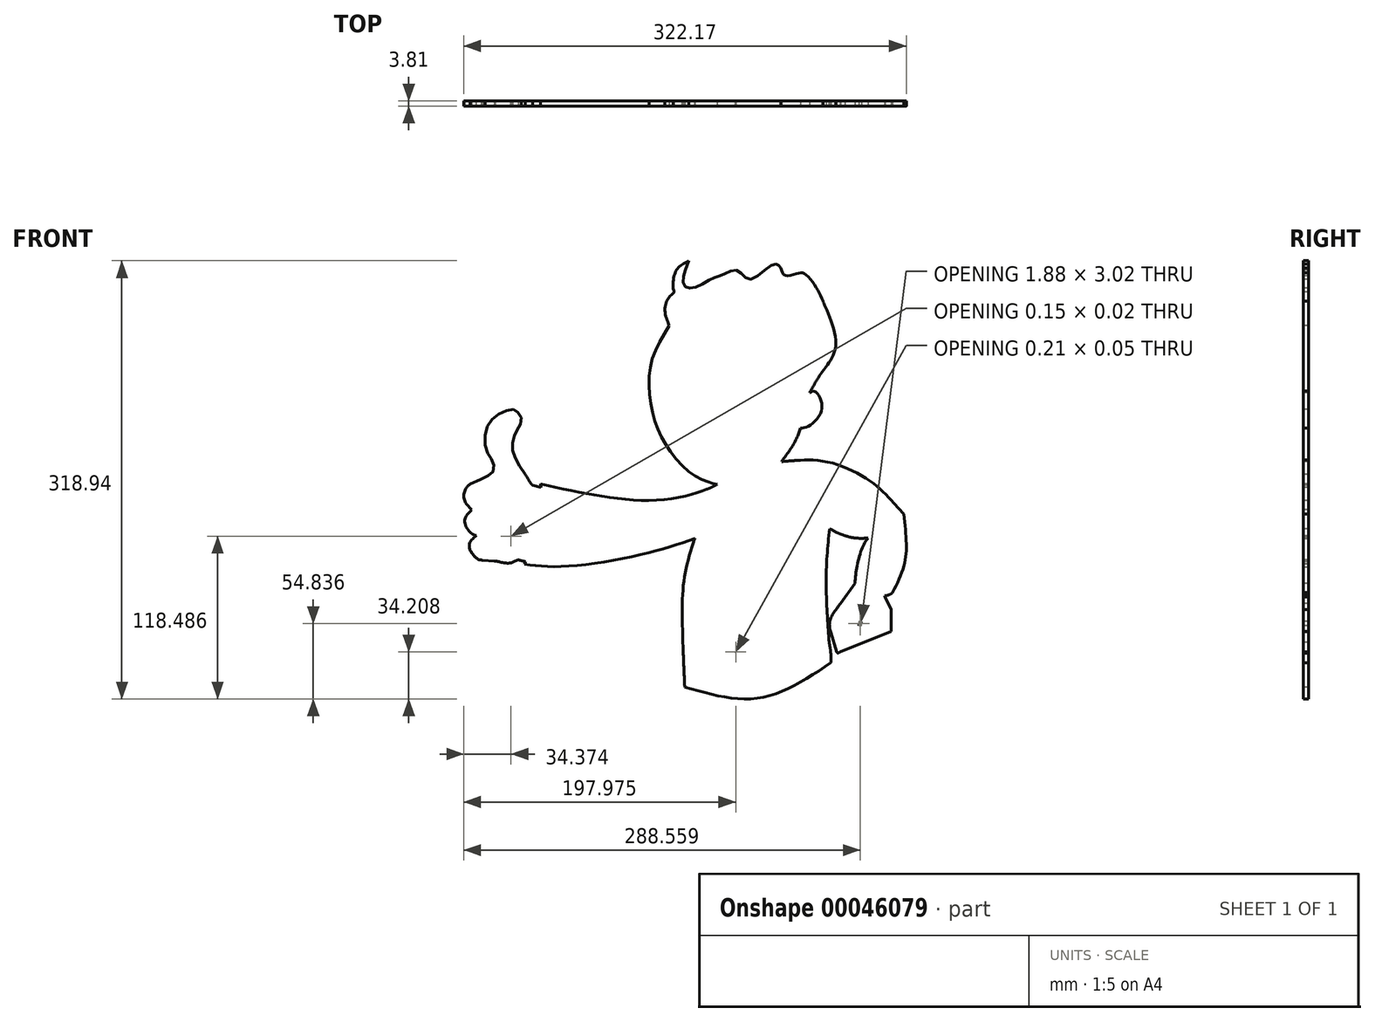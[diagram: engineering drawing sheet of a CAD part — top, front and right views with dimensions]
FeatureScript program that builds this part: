
annotation { "Feature Type Name" : "Feature", "Feature Type Description" : "" }
export const myFeature = defineFeature(function(context is Context, id is Id, definition is map)
    precondition{}
    {
        {
            var Q0;
            Q0=qCreatedBy(makeId("Front.planeOp"),FACE);
            var sketch = newSketch(context, id + "F0", { "sketchPlane" : qUnion([Q0])});
            skFitSpline(sketch, "E0", {"points": [v(50.13, 110.54) * mm, v(59.42, 125.93) * mm, v(69.05, 147.45) * mm, v(59.82, 176.78) * mm, v(59.82, 177.15) * mm], "startDerivative": vector(29.75, 55.27) * mm, "endDerivative": vector(2.31, 5.04) * mm});
            skFitSpline(sketch, "E1", {"points": [v(-32.08, 166.14) * mm, v(-26.7, 166.14) * mm, v(-15.06, 171.52) * mm, v(-4.76, 175.55) * mm, v(2.41, 166.14) * mm, v(16.75, 170.18) * mm, v(24.81, 173.31) * mm, v(31.08, 166.14) * mm, v(33.77, 158.53) * mm, v(35.56, 153.6) * mm, v(48.1, 156.29) * mm, v(57.52, 154.05) * mm, v(51.25, 141.5) * mm, v(44.08, 133.89) * mm], "startDerivative": vector(88.2, -10.9) * mm, "endDerivative": vector(-84.16, -80.95) * mm});
            skFitSpline(sketch, "E2", {"points": [v(44.08, 133.89) * mm, v(54.38, 133.89) * mm, v(62.92, 130.58) * mm], "startDerivative": vector(20.66, 1.85) * mm, "endDerivative": vector(16.64, -8.92) * mm});
            skFitSpline(sketch, "E3", {"points": [v(-47.44, 143.12) * mm, v(-53.66, 138) * mm, v(-54.76, 129.95) * mm, v(-52.93, 123) * mm, v(-47.22, 118.56) * mm, v(-41.77, 124.33) * mm, v(-40.65, 130.58) * mm, v(-42.1, 138.75) * mm, v(-47.44, 143.12) * mm]});
            skFitSpline(sketch, "E4", {"points": [v(-0.6, 133.82) * mm, v(6.36, 138.75) * mm, v(18.44, 133.82) * mm, v(22.47, 129.22) * mm], "startDerivative": vector(18.6, 18.3) * mm, "endDerivative": vector(10.5, -16.47) * mm});
            skFitSpline(sketch, "E5", {"points": [v(-0.6, 133.82) * mm, v(-1.4, 132.75) * mm, v(-0.6, 131.78) * mm, v(1.27, 132.99) * mm, v(2.15, 133.82) * mm, v(3.6, 135.16) * mm, v(6.5, 136.21) * mm, v(11.42, 135.4) * mm, v(15.2, 133.82) * mm], "startDerivative": vector(-12.6, -10.27) * mm, "endDerivative": vector(21.53, -10.19) * mm});
            skFitSpline(sketch, "E6", {"points": [v(15.2, 133.82) * mm, v(16.01, 133.23) * mm, v(19.24, 130.4) * mm, v(20.69, 128.88) * mm, v(21.74, 128.4) * mm, v(22.47, 129.22) * mm], "startDerivative": vector(4.24, -2.9) * mm, "endDerivative": vector(4.07, 7.17) * mm});
            skFitSpline(sketch, "E7", {"points": [v(-21.75, 134.43) * mm, v(-25.48, 123.23) * mm, v(-35.27, 105.04) * mm, v(-35.97, 103.17) * mm, v(-35.27, 100.37) * mm, v(-32.24, 96.64) * mm, v(-31.3, 94.77) * mm], "startDerivative": vector(-10.07, -41.5) * mm, "endDerivative": vector(6.38, -17.85) * mm});
            skFitSpline(sketch, "E8", {"points": [v(-21.75, 134.43) * mm, v(-24.78, 119.73) * mm, v(-28.74, 108.77) * mm, v(-29.44, 103.4) * mm], "startDerivative": vector(-5.78, -37.33) * mm, "endDerivative": vector(-0.9, -20.57) * mm});
            skFitSpline(sketch, "E9", {"points": [v(-29.44, 103.4) * mm, v(-24.31, 96.87) * mm], "startDerivative": vector(5.13, -6.53) * mm, "endDerivative": vector(5.13, -6.53) * mm});
            skFitSpline(sketch, "E10", {"points": [v(-35.27, 82.18) * mm, v(-36.67, 76.11) * mm, v(-33.18, 65.15) * mm, v(-42.04, 73.55) * mm, v(-35.27, 82.18) * mm]});
            skLineSegment(sketch, "E11", {"start": v(-24.31, 96.87) * mm, "end": v(-31.3, 94.77) * mm});
            skFitSpline(sketch, "E12", {"points": [v(-36.33, 78.76) * mm, v(-18.4, 77.61) * mm, v(-2.48, 81.02) * mm, v(-2.48, 81.11) * mm], "startDerivative": vector(32.43, -5.7) * mm, "endDerivative": vector(-1.31, 2.33) * mm});
            skFitSpline(sketch, "E13", {"points": [v(-33.18, 66.5) * mm, v(-27.23, 65.15) * mm, v(-7.82, 65.15) * mm, v(7.83, 73.93) * mm], "startDerivative": vector(22, -6.15) * mm, "endDerivative": vector(37.03, 28.65) * mm});
            skFitSpline(sketch, "E14", {"points": [v(-2.46, 81.08) * mm, v(1.2, 82.95) * mm], "startDerivative": vector(3.67, 1.87) * mm, "endDerivative": vector(3.67, 1.87) * mm});
            skFitSpline(sketch, "E15", {"points": [v(1.2, 82.95) * mm, v(1.2, 84.33) * mm, v(2.12, 86.63) * mm, v(4.42, 86.82) * mm, v(8.56, 85.07) * mm, v(11.42, 83.87) * mm, v(13.53, 79.91) * mm, v(13.35, 75.77) * mm, v(12.52, 73.38) * mm, v(11.42, 74.67) * mm, v(11.42, 76.88) * mm, v(10.87, 79.73) * mm, v(10.04, 81.02) * mm, v(5.34, 82.3) * mm, v(1.2, 82.95) * mm]});
            skFitSpline(sketch, "E16", {"points": [v(7.83, 73.93) * mm, v(10.59, 76.88) * mm], "startDerivative": vector(2.76, 2.94) * mm, "endDerivative": vector(2.76, 2.94) * mm});
            skFitSpline(sketch, "E17", {"points": [v(60.14, 126.9) * mm, v(56.3, 128.64) * mm, v(46.2, 131) * mm, v(44.44, 130.67) * mm, v(44.1, 129.59) * mm, v(45.05, 129.31) * mm, v(48.5, 128.64) * mm, v(54.26, 127.35) * mm, v(58.83, 125.11) * mm], "startDerivative": vector(-22.37, 12.58) * mm, "endDerivative": vector(29.2, -17) * mm});
            skFitSpline(sketch, "E18", {"points": [v(57.45, 123.12) * mm, v(56.23, 124.5) * mm, v(49.05, 126.6) * mm, v(46.2, 126.94) * mm, v(45.66, 126.2) * mm, v(46.33, 125.25) * mm, v(49.11, 124.77) * mm, v(54.13, 123.62) * mm, v(56.59, 121.8) * mm], "startDerivative": vector(-7.37, 14.27) * mm, "endDerivative": vector(16.28, -15.48) * mm});
            skFitSpline(sketch, "E19", {"points": [v(45.72, 119.76) * mm, v(44.3, 120.03) * mm, v(44.44, 121.18) * mm, v(47.83, 121.18) * mm, v(50.33, 120.44) * mm, v(51.55, 119.49) * mm, v(51.82, 118.4) * mm, v(50.67, 118.13) * mm, v(49.25, 118.95) * mm, v(47.42, 119.42) * mm, v(45.72, 119.76) * mm]});
            skFitSpline(sketch, "E20", {"points": [v(42.81, 115.67) * mm, v(45.72, 115.67) * mm, v(49.45, 114) * mm], "startDerivative": vector(6.25, 0.7) * mm, "endDerivative": vector(7.01, -3.9) * mm});
            skFitSpline(sketch, "E21", {"points": [v(42.81, 115.67) * mm, v(42.2, 115.08) * mm, v(42.81, 114.88) * mm, v(43.76, 114.88) * mm, v(44.84, 114.95) * mm, v(46.06, 114.81) * mm, v(48.18, 114) * mm, v(48.97, 113.67) * mm, v(49.45, 113.74) * mm, v(49.45, 114) * mm], "startDerivative": vector(-8.93, -6.16) * mm, "endDerivative": vector(-1.3, 4.9) * mm});
            skFitSpline(sketch, "E22", {"points": [v(-15.65, 58.15) * mm, v(-11.91, 58.75) * mm, v(-6.83, 60.7) * mm, v(-5.63, 59.5) * mm, v(-5.04, 57.7) * mm, v(-7.28, 57.1) * mm, v(-11.02, 57.1) * mm, v(-15.65, 58.15) * mm]});
            skFitSpline(sketch, "E23", {"points": [v(-53.58, 144.28) * mm, v(-52.5, 144.07) * mm, v(-48.8, 146.02) * mm, v(-42.6, 149.29) * mm, v(-39.22, 150.38) * mm], "startDerivative": vector(7.02, -3.06) * mm, "endDerivative": vector(12.56, 3.33) * mm});
            skFitSpline(sketch, "E24", {"points": [v(-53.58, 144.28) * mm, v(-53.58, 145.26) * mm, v(-44.66, 150.38) * mm], "startDerivative": vector(-1.38, 3.85) * mm, "endDerivative": vector(16.14, 7.66) * mm});
            skFitSpline(sketch, "E25", {"points": [v(-44.66, 150.38) * mm, v(-39.44, 152.34) * mm, v(-37.92, 151.9) * mm, v(-37.59, 151.25) * mm, v(-39.22, 150.38) * mm], "startDerivative": vector(14.6, 6.93) * mm, "endDerivative": vector(-9.7, -3.42) * mm});
            skFitSpline(sketch, "E26", {"points": [v(8.7, 154.3) * mm, v(7.32, 153.67) * mm, v(6.69, 152.22) * mm, v(6.82, 151.03) * mm, v(7, 150.97) * mm], "startDerivative": vector(-5.03, -1.45) * mm, "endDerivative": vector(1.83, 0) * mm});
            skFitSpline(sketch, "E27", {"points": [v(7, 150.97) * mm, v(7.82, 150.46) * mm, v(10.78, 150.09) * mm, v(14.04, 148.96) * mm, v(16.94, 147.07) * mm, v(19.45, 144.74) * mm, v(20.96, 142.86) * mm, v(22.72, 143.68) * mm, v(22.15, 145.62) * mm, v(20.2, 148.64) * mm, v(17.5, 150.97) * mm, v(13.98, 153.48) * mm, v(10.27, 154.61) * mm, v(8.7, 154.3) * mm], "startDerivative": vector(14.48, -12.75) * mm, "endDerivative": vector(-23.85, -8.4) * mm});
            skFitSpline(sketch, "E28", {"points": [v(-17.29, 43.67) * mm, v(-14.75, 40.26) * mm, v(0.53, 36.43) * mm, v(24.24, 42.28) * mm, v(29.61, 55.12) * mm, v(29.61, 60.02) * mm], "startDerivative": vector(13.91, -29.26) * mm, "endDerivative": vector(-2.2, 31.94) * mm});
            skFitSpline(sketch, "E29", {"points": [v(29.61, 60.02) * mm, v(29.61, 60.9) * mm], "startDerivative": vector(0, 0.88) * mm, "endDerivative": vector(0, 0.88) * mm});
            skFitSpline(sketch, "E30", {"points": [v(-33.78, 4) * mm, v(-40.9, -22.22) * mm, v(-42.7, -53.76) * mm, v(-40.9, -103.78) * mm], "startDerivative": vector(-28.62, -88.9) * mm, "endDerivative": vector(6.18, -133.53) * mm});
            skFitSpline(sketch, "E31", {"points": [v(64.54, 11.47) * mm, v(62.05, -23.4) * mm, v(64.23, -71.35) * mm], "startDerivative": vector(-7.58, -72.7) * mm, "endDerivative": vector(6.59, -92.41) * mm});
            skFitSpline(sketch, "E32", {"points": [v(29.61, 60.31) * mm, v(37.36, 60.9) * mm, v(61.6, 60.31) * mm, v(94.7, 45.73) * mm, v(111.2, 30.12) * mm], "startDerivative": vector(44.64, 3.25) * mm, "endDerivative": vector(55.06, -61.44) * mm});
            skFitSpline(sketch, "E33", {"points": [v(75.86, 6.32) * mm, v(82.98, 4.7) * mm, v(92.43, 4.6) * mm], "startDerivative": vector(14.64, -4.26) * mm, "endDerivative": vector(18.43, 0.72) * mm});
            skFitSpline(sketch, "E34", {"points": [v(111.2, 30.12) * mm, v(118.49, 22.03) * mm], "startDerivative": vector(7.3, -8.1) * mm, "endDerivative": vector(7.3, -8.1) * mm});
            skFitSpline(sketch, "E35", {"points": [v(92.43, 4.6) * mm, v(89.16, -0.64) * mm, v(84.7, -14.75) * mm, v(82.98, -28.23) * mm], "startDerivative": vector(-13.12, -17.8) * mm, "endDerivative": vector(-2.92, -35.34) * mm});
            skFitSpline(sketch, "E36", {"points": [v(82.98, -28.23) * mm, v(72.5, -42.99) * mm], "startDerivative": vector(-10.48, -14.76) * mm, "endDerivative": vector(-10.48, -14.76) * mm});
            skFitSpline(sketch, "E37", {"points": [v(65.44, -64.38) * mm, v(69.72, -78.18) * mm], "startDerivative": vector(4.28, -13.8) * mm, "endDerivative": vector(4.28, -13.8) * mm});
            skFitSpline(sketch, "E38", {"points": [v(72.33, -78.18) * mm, v(109.5, -63.22) * mm], "startDerivative": vector(37.16, 14.96) * mm, "endDerivative": vector(37.16, 14.96) * mm});
            skFitSpline(sketch, "E39", {"points": [v(109.5, -63.22) * mm, v(109.5, -47.36) * mm], "startDerivative": vector(0, 15.86) * mm, "endDerivative": vector(0, 15.86) * mm});
            skFitSpline(sketch, "E40", {"points": [v(109.5, -47.36) * mm, v(104.96, -38.07) * mm], "startDerivative": vector(-4.53, 9.3) * mm, "endDerivative": vector(-4.53, 9.3) * mm});
            skFitSpline(sketch, "E41", {"points": [v(104.77, -41.17) * mm, v(91.36, -50.08) * mm, v(91.36, -50.53) * mm], "startDerivative": vector(-22.36, -13.52) * mm, "endDerivative": vector(1.12, -2.63) * mm});
            skFitSpline(sketch, "E42", {"points": [v(91.36, -50.08) * mm, v(85.93, -59.14) * mm], "startDerivative": vector(-5.44, -9.06) * mm, "endDerivative": vector(-5.44, -9.06) * mm});
            skFitSpline(sketch, "E43", {"points": [v(87.74, -56.12) * mm, v(85.93, -59.14) * mm, v(95, -59.14) * mm], "startDerivative": vector(-8.45, -9.38) * mm, "endDerivative": vector(20.7, 2.42) * mm});
            skFitSpline(sketch, "E44", {"points": [v(95, -58.7) * mm, v(98.62, -52.8) * mm], "startDerivative": vector(3.63, 5.9) * mm, "endDerivative": vector(3.63, 5.9) * mm});
            skFitSpline(sketch, "E45", {"points": [v(105.06, -38.26) * mm, v(104.56, -37.13) * mm], "startDerivative": vector(-0.5, 1.13) * mm, "endDerivative": vector(-0.5, 1.13) * mm});
            skFitSpline(sketch, "E46", {"points": [v(69.72, -78.18) * mm, v(70.41, -79) * mm, v(72.33, -78.18) * mm], "startDerivative": vector(1.32, -2.65) * mm, "endDerivative": vector(3.77, 2.37) * mm});
            skFitSpline(sketch, "E47", {"points": [v(110.17, -33.85) * mm, v(110.16, -33.84) * mm], "startDerivative": vector(0, 0) * mm, "endDerivative": vector(0, 0) * mm});
            skFitSpline(sketch, "E48", {"points": [v(-33.78, 4) * mm, v(-33.57, 4.26) * mm], "startDerivative": vector(0.18, 0.3) * mm, "endDerivative": vector(0.18, 0.3) * mm});
            skFitSpline(sketch, "E49", {"points": [v(-40.9, -103.78) * mm, v(13.5, -111.72) * mm, v(65.41, -86.24) * mm], "startDerivative": vector(112.06, -32.49) * mm, "endDerivative": vector(100.6, 67.15) * mm});
            skFitSpline(sketch, "E50", {"points": [v(64.23, -71.35) * mm, v(65.41, -79) * mm, v(65.41, -86.24) * mm], "startDerivative": vector(2.92, -15.13) * mm, "endDerivative": vector(-0.57, -14.64) * mm});
            skFitSpline(sketch, "E51", {"points": [v(-42.13, -75) * mm, v(-16.18, -79.13) * mm, v(27.63, -70.95) * mm, v(52.32, -59.13) * mm, v(62.83, -50.46) * mm], "startDerivative": vector(94.94, -25.3) * mm, "endDerivative": vector(54.09, 48.22) * mm});
            skFitSpline(sketch, "E52", {"points": [v(-41.47, -91.12) * mm, v(-18.12, -96.3) * mm, v(18.32, -93.46) * mm, v(50.3, -79.94) * mm, v(64.52, -72.9) * mm], "startDerivative": vector(92.5, -27.07) * mm, "endDerivative": vector(66.9, 32.65) * mm});
            skFitSpline(sketch, "E53", {"points": [v(0.53, 26.25) * mm, v(-4.3, 0.08) * mm, v(-8.09, -30.58) * mm, v(-5.36, -64.6) * mm, v(-3.68, -78.24) * mm, v(-3.89, -78.27) * mm], "startDerivative": vector(-19.33, -103.38) * mm, "endDerivative": vector(-10.4, 2.62) * mm});
            skFitSpline(sketch, "E54", {"points": [v(21.54, 27.5) * mm, v(16.27, 5.96) * mm, v(13.12, -17.56) * mm, v(11.44, -35) * mm, v(12.91, -52.84) * mm, v(16.48, -74.27) * mm], "startDerivative": vector(-28.05, -100.99) * mm, "endDerivative": vector(18.76, -106.08) * mm});
            skFitSpline(sketch, "E55", {"points": [v(43.22, 61.3) * mm, v(42.44, 49.4) * mm, v(33.94, 36.02) * mm, v(21.54, 27.5) * mm], "startDerivative": vector(2.05, -38.27) * mm, "endDerivative": vector(-37.8, -21.41) * mm});
            skFitSpline(sketch, "E56", {"points": [v(-145.77, 44.08) * mm, v(-99.83, 34.78) * mm, v(-53.62, 32.83) * mm, v(-24.87, 40.17) * mm, v(-17.29, 43.67) * mm], "startDerivative": vector(145.84, -33.23) * mm, "endDerivative": vector(48.2, 24.73) * mm});
            skFitSpline(sketch, "E57", {"points": [v(-156.74, -12.52) * mm, v(-161.16, -11.46) * mm, v(-162.17, -11.16) * mm], "startDerivative": vector(-7.13, 1.61) * mm, "endDerivative": vector(-2.2, -0.18) * mm});
            skFitSpline(sketch, "E58", {"points": [v(-145.53, 41.63) * mm, v(-151.61, 42.93) * mm], "startDerivative": vector(-5.81, 1.25) * mm, "endDerivative": vector(-5.81, 1.25) * mm});
            skFitSpline(sketch, "E59", {"points": [v(-152.1, 13.65) * mm, v(-152.56, 13.96) * mm, v(-153.22, 14.24) * mm], "startDerivative": vector(-0.82, 0.82) * mm, "endDerivative": vector(-1.34, 0.38) * mm});
            skFitSpline(sketch, "E60", {"points": [v(-153.22, 14.24) * mm, v(-152.6, 14.2) * mm, v(-151.54, 14.49) * mm], "startDerivative": vector(1.37, -0.2) * mm, "endDerivative": vector(1.96, 0.66) * mm});
            skFitSpline(sketch, "E61", {"points": [v(-189, -11.33) * mm, v(-192.36, -10.14) * mm, v(-197.81, -1.13) * mm, v(-192.6, 6.51) * mm], "startDerivative": vector(-13.42, -0.8) * mm, "endDerivative": vector(21.15, 18.09) * mm});
            skFitSpline(sketch, "E62", {"points": [v(-192.6, 6.51) * mm, v(-195.44, 7.4) * mm, v(-201.13, 16.66) * mm, v(-195.91, 25.24) * mm], "startDerivative": vector(-11.37, -0.03) * mm, "endDerivative": vector(20.78, 19.91) * mm});
            skFitSpline(sketch, "E63", {"points": [v(-151.54, 14.49) * mm, v(-150.68, 14.7) * mm, v(-148.1, 19.04) * mm, v(-147.1, 25.9) * mm, v(-147.4, 37.26) * mm, v(-147.4, 37.4) * mm], "startDerivative": vector(8.17, -0.43) * mm, "endDerivative": vector(0.09, 1.86) * mm});
            skFitSpline(sketch, "E64", {"points": [v(-147.4, 37.4) * mm, v(-147.8, 39.01) * mm, v(-149.54, 41.18) * mm, v(-151.61, 42.93) * mm], "startDerivative": vector(-0.72, 5.61) * mm, "endDerivative": vector(-5.82, 4.56) * mm});
            skFitSpline(sketch, "E65", {"points": [v(-151.61, 42.93) * mm, v(-152.66, 44.09) * mm, v(-157.02, 51) * mm], "startDerivative": vector(-2.81, 2.98) * mm, "endDerivative": vector(-7.66, 11.82) * mm});
            skFitSpline(sketch, "E66", {"points": [v(-197.17, 43.98) * mm, v(-183.66, 50.12) * mm, v(-179.9, 54.02) * mm, v(-180.97, 61.15) * mm, v(-184.47, 66.4) * mm, v(-186.22, 78.5) * mm, v(-182.45, 89.53) * mm, v(-174.51, 95.85) * mm, v(-165.9, 98.23) * mm, v(-162.03, 95.69) * mm, v(-159.84, 90.86) * mm, v(-162.3, 84.42) * mm, v(-165.04, 78.84) * mm, v(-166.36, 71.37) * mm, v(-164.2, 62.86) * mm, v(-157.02, 51) * mm], "startDerivative": vector(180.37, 86.36) * mm, "endDerivative": vector(95.72, -136.07) * mm});
            skFitSpline(sketch, "E67", {"points": [v(-195.91, 25.24) * mm, v(-170.12, 24.3) * mm], "startDerivative": vector(25.8, -0.95) * mm, "endDerivative": vector(25.8, -0.95) * mm});
            skFitSpline(sketch, "E68", {"points": [v(-166.9, 24.18) * mm, v(-161.58, 21.84) * mm, v(-160.2, 11.2) * mm, v(-164.29, 6.67) * mm, v(-192.6, 6.51) * mm], "startDerivative": vector(33.91, -4.89) * mm, "endDerivative": vector(-87.46, 5.9) * mm});
            skFitSpline(sketch, "E69", {"points": [v(-192.6, 6.51) * mm, v(-167.46, 6) * mm, v(-167.31, 6.03) * mm], "startDerivative": vector(38.67, -0.96) * mm, "endDerivative": vector(1.14, 0.36) * mm});
            skFitSpline(sketch, "E70", {"points": [v(-197.17, 43.98) * mm, v(-197.16, 43.92) * mm, v(-197.21, 43.96) * mm], "startDerivative": vector(-0.03, -0.02) * mm, "endDerivative": vector(-0.05, -0.03) * mm});
            skFitSpline(sketch, "E71", {"points": [v(-166.9, 24.18) * mm, v(-167.19, 24.16) * mm, v(-167.4, 24.24) * mm], "startDerivative": vector(-0.57, 0.07) * mm, "endDerivative": vector(-0.4, 0.06) * mm});
            skFitSpline(sketch, "E72", {"points": [v(-37.9, 206.47) * mm, v(-40.58, 199.07) * mm, v(-41.45, 188.92) * mm, v(-35.07, 186.6) * mm, v(-21.44, 193.27) * mm, v(-12.45, 196.75) * mm, v(-2.59, 199.36) * mm, v(5.83, 192.98) * mm, v(21.78, 202.84) * mm, v(27, 203.42) * mm, v(29.03, 201.1) * mm], "startDerivative": vector(-28.8, -72.3) * mm, "endDerivative": vector(29.74, -46.45) * mm});
            skFitSpline(sketch, "E73", {"points": [v(29.03, 201.1) * mm, v(32.22, 195.88) * mm, v(41.8, 197.33) * mm, v(46.14, 197.04) * mm, v(54.26, 188.05) * mm, v(59.82, 177.15) * mm], "startDerivative": vector(11.35, -40.23) * mm, "endDerivative": vector(19.55, -44.97) * mm});
            skFitSpline(sketch, "E74", {"points": [v(-189, -11.33) * mm, v(-188.14, -11.56) * mm], "startDerivative": vector(0.85, -0.29) * mm, "endDerivative": vector(0.85, -0.29) * mm});
            skFitSpline(sketch, "E75", {"points": [v(-179.52, -12.07) * mm, v(-178.5, -12.07) * mm, v(-169.81, -13.61) * mm, v(-161.93, -11.14) * mm], "startDerivative": vector(6.5, 0.95) * mm, "endDerivative": vector(24.22, 10.12) * mm});
            skFitSpline(sketch, "E76", {"points": [v(-161.93, -11.14) * mm, v(-155.9, -6.95) * mm, v(-153.19, -2.2) * mm, v(-151.97, 5.81) * mm, v(-152.1, 13.65) * mm], "startDerivative": vector(21.28, 21.91) * mm, "endDerivative": vector(-1.06, 28.7) * mm});
            skFitSpline(sketch, "E77", {"points": [v(-24.87, 40.17) * mm, v(-22.24, 35.54) * mm, v(-8.09, 27.34) * mm, v(0.53, 26.25) * mm], "startDerivative": vector(5.88, -17.7) * mm, "endDerivative": vector(24.32, 0.18) * mm});
            skFitSpline(sketch, "E78", {"points": [v(-32.08, 166.14) * mm, v(-36.7, 167.93) * mm, v(-41.64, 170.56) * mm], "startDerivative": vector(-9.85, 2.76) * mm, "endDerivative": vector(-7.14, 8.19) * mm});
            skFitSpline(sketch, "E79", {"points": [v(-48.62, 183.8) * mm, v(-52, 180.15) * mm, v(-55.34, 169.96) * mm, v(-52.23, 159.14) * mm], "startDerivative": vector(-7.04, -13.73) * mm, "endDerivative": vector(5.31, -16.1) * mm});
            skFitSpline(sketch, "E80", {"points": [v(-197.16, 43.92) * mm, v(-200.07, 40.94) * mm, v(-201.59, 33.35) * mm, v(-195.91, 25.24) * mm], "startDerivative": vector(-11.93, -9.3) * mm, "endDerivative": vector(19.13, -19.37) * mm});
            skFitSpline(sketch, "E81", {"points": [v(-197.16, 43.92) * mm, v(-175, 43.92) * mm, v(-164.96, 40.84) * mm, v(-160.78, 30.34) * mm, v(-164.73, 25.15) * mm, v(-166.9, 24.18) * mm, v(-170.12, 24.3) * mm], "startDerivative": vector(88.21, 1.7) * mm, "endDerivative": vector(-33.47, 3.56) * mm});
            skFitSpline(sketch, "E82", {"points": [v(-145.77, 44.08) * mm, v(-145.53, 41.63) * mm], "startDerivative": vector(0.23, -2.45) * mm, "endDerivative": vector(0.23, -2.45) * mm});
            skFitSpline(sketch, "E83", {"points": [v(-157.65, -14.45) * mm, v(-156.74, -12.52) * mm], "startDerivative": vector(0.92, 1.93) * mm, "endDerivative": vector(0.92, 1.93) * mm});
            skFitSpline(sketch, "E84", {"points": [v(-156.74, -12.52) * mm, v(-149.44, 0) * mm, v(-144.45, 13.1) * mm, v(-145.53, 41.63) * mm], "startDerivative": vector(25.63, 42.98) * mm, "endDerivative": vector(-8.16, 75.99) * mm});
            skFitSpline(sketch, "E85", {"points": [v(75.86, 6.32) * mm, v(71.26, 8.02) * mm, v(64.54, 11.47) * mm], "startDerivative": vector(-9.9, 3.26) * mm, "endDerivative": vector(-12.64, 6.9) * mm});
            skFitSpline(sketch, "E86", {"points": [v(64.54, 11.47) * mm, v(63.72, 12.05) * mm, v(61.99, 13.69) * mm], "startDerivative": vector(-1.93, 1.25) * mm, "endDerivative": vector(-3.09, 3.06) * mm});
            skFitSpline(sketch, "E87", {"points": [v(72.5, -42.99) * mm, v(68.2, -48.82) * mm, v(64.59, -56.32) * mm, v(65.44, -64.38) * mm], "startDerivative": vector(-13.37, -17.43) * mm, "endDerivative": vector(5.8, -24.1) * mm});
            skFitSpline(sketch, "E88", {"points": [v(104.77, -41.17) * mm, v(105.75, -40.64) * mm, v(106.47, -41.17) * mm], "startDerivative": vector(1.95, 1.54) * mm, "endDerivative": vector(1.44, -1.6) * mm});
            skFitSpline(sketch, "E89", {"points": [v(-157.65, -14.45) * mm, v(-128.26, -15.97) * mm, v(-68.84, -6.4) * mm, v(-33.57, 4.26) * mm], "startDerivative": vector(92.4, -11.33) * mm, "endDerivative": vector(100.31, 34.14) * mm});
            skFitSpline(sketch, "E90", {"points": [v(82.98, -28.23) * mm, v(85.19, -30.53) * mm, v(95.75, -34.92) * mm, v(104.56, -37.13) * mm], "startDerivative": vector(7.12, -10.3) * mm, "endDerivative": vector(22.19, -4.83) * mm});
            skFitSpline(sketch, "E91", {"points": [v(104.56, -37.13) * mm, v(106.4, -37.13) * mm, v(109.68, -35.69) * mm, v(110.45, -35.04) * mm], "startDerivative": vector(5.08, -0.79) * mm, "endDerivative": vector(2.4, 2.48) * mm});
            skFitSpline(sketch, "E92", {"points": [v(118.49, 22.03) * mm, v(120.4, 0) * mm, v(118.49, -16.17) * mm, v(110.45, -35.04) * mm], "startDerivative": vector(7.53, -64.86) * mm, "endDerivative": vector(-27.6, -56.45) * mm});
            skFitSpline(sketch, "E93", {"points": [v(43.38, 84.78) * mm, v(39.44, 74.98) * mm, v(29.61, 60.31) * mm], "startDerivative": vector(-7.22, -21.7) * mm, "endDerivative": vector(-19.79, -27.01) * mm});
            skFitSpline(sketch, "E94", {"points": [v(29.61, 60.31) * mm, v(28.9, 59.33) * mm, v(27.2, 58.02) * mm, v(27.18, 58) * mm], "startDerivative": vector(-1.06, -2.15) * mm, "endDerivative": vector(-0.08, -0.13) * mm});
            skFitSpline(sketch, "E95", {"points": [v(-17.29, 43.67) * mm, v(-23.81, 45.38) * mm, v(-37.25, 52.37) * mm, v(-53.03, 70.12) * mm, v(-62.52, 89.43) * mm, v(-66.83, 113.26) * mm, v(-64, 136.56) * mm, v(-52.23, 159.14) * mm], "startDerivative": vector(-71.14, 15.45) * mm, "endDerivative": vector(78.93, 135.15) * mm});
            skFitSpline(sketch, "E96", {"points": [v(-52.23, 159.14) * mm, v(-46.86, 166.35) * mm, v(-41.64, 170.56) * mm], "startDerivative": vector(9.66, 14.61) * mm, "endDerivative": vector(11.57, 8.08) * mm});
            skFitSpline(sketch, "E97", {"points": [v(-17.29, 43.67) * mm, v(-12.79, 43.12) * mm, v(-10.72, 43.08) * mm], "startDerivative": vector(4.13, -1.26) * mm, "endDerivative": vector(3.89, -0.12) * mm});
            skFitSpline(sketch, "E98", {"points": [v(50.13, 110.54) * mm, v(53.61, 111.45) * mm, v(58.27, 105.04) * mm, v(57.6, 94.74) * mm, v(48.8, 85.84) * mm, v(43.38, 84.78) * mm], "startDerivative": vector(24.96, 14.11) * mm, "endDerivative": vector(-29.77, -0.66) * mm});
            skFitSpline(sketch, "E99", {"points": [v(50.13, 110.54) * mm, v(48.62, 109.78) * mm, v(47.13, 108.54) * mm, v(46.8, 107.95) * mm], "startDerivative": vector(-3.96, -1.72) * mm, "endDerivative": vector(-0.97, -2.31) * mm});
            skLineSegment(sketch, "E100", {"start": v(-188.14, -11.56) * mm, "end": v(-179.52, -12.07) * mm});
            skLineSegment(sketch, "E101", {"start": v(-179.2, -12.03) * mm, "end": v(-166.1, -12.07) * mm});
            skFitSpline(sketch, "E102", {"points": [v(-167.3, 6.03) * mm, v(-162.34, 4.76) * mm, v(-160.76, -2.98) * mm, v(-162.1, -8.55) * mm, v(-166.1, -12.07) * mm], "startDerivative": vector(24.78, -0.12) * mm, "endDerivative": vector(-19.59, -13.52) * mm});
            skFitSpline(sketch, "E103", {"points": [v(-37.9, 206.47) * mm, v(-45.23, 201.8) * mm, v(-48.22, 196.8) * mm, v(-49.5, 187.52) * mm, v(-48.62, 183.8) * mm], "startDerivative": vector(-29.17, -15.9) * mm, "endDerivative": vector(6.26, -16.7) * mm});
            skFitSpline(sketch, "E104", {"points": [v(-48.62, 183.8) * mm, v(-47.15, 179.74) * mm, v(-43.2, 172.92) * mm, v(-41.64, 170.56) * mm], "startDerivative": vector(3.33, -11.6) * mm, "endDerivative": vector(5.22, -7.62) * mm});
            skSolve(sketch);
        }
        {
            var Q0;
            Q0 = qSketchRegion(id + "F0", true);
            extrude(context, id + "F1", {"entities" : qUnion([Q0]), "oppositeDirection" : true, "depth" : 3.8 * mm});
        }
        {
            var Q0;
            {var subQ0=sQuery(id+"F0.wireOp",EDGE,"E10");var subQ1=makeQuery(id+"F0.imprint","IMPRINT",VERTEX,{"disambiguationData":[OD(0.0)],"derivedFrom":subQ0});Q0=makeQuery(id+"F0.imprint","IMPRINT",FACE,{"disambiguationData":[TD([[makeQuery(id+"F0.imprint","IMPRINT",EDGE,{"disambiguationData":[TD([[subQ1,-1.0]])],"derivedFrom":subQ0}),-1.0]])]});}
            var Q1;
            Q1=makeQuery(id+"F0.imprint","IMPRINT",FACE,{"disambiguationData":[TD([[makeQuery(id+"F0.imprint","IMPRINT",EDGE,{"derivedFrom":sQuery(id+"F0.wireOp",EDGE,"E22")}),-1.0]])]});
            var Q2;
            Q2=makeQuery(id+"F0.imprint","IMPRINT",FACE,{"disambiguationData":[TD([[makeQuery(id+"F0.imprint","IMPRINT",EDGE,{"derivedFrom":sQuery(id+"F0.wireOp",EDGE,"E15")}),-1.0]])]});
            var Q3;
            Q3=makeQuery(id+"F0.imprint","IMPRINT",FACE,{"disambiguationData":[TD([[makeQuery(id+"F0.imprint","IMPRINT",EDGE,{"derivedFrom":sQuery(id+"F0.wireOp",EDGE,"E7")}),1.0]])]});
            var Q4;
            Q4=makeQuery(id+"F0.imprint","IMPRINT",FACE,{"disambiguationData":[TD([[makeQuery(id+"F0.imprint","IMPRINT",EDGE,{"derivedFrom":sQuery(id+"F0.wireOp",EDGE,"E20")}),-1.0]])]});
            var Q5;
            Q5=makeQuery(id+"F0.imprint","IMPRINT",FACE,{"disambiguationData":[TD([[makeQuery(id+"F0.imprint","IMPRINT",EDGE,{"derivedFrom":sQuery(id+"F0.wireOp",EDGE,"E19")}),-1.0]])]});
            var Q6;
            Q6=makeQuery(id+"F0.imprint","IMPRINT",FACE,{"disambiguationData":[TD([[makeQuery(id+"F0.imprint","IMPRINT",EDGE,{"derivedFrom":sQuery(id+"F0.wireOp",EDGE,"E4")}),-1.0]])]});
            var Q7;
            Q7=makeQuery(id+"F0.imprint","IMPRINT",FACE,{"disambiguationData":[TD([[makeQuery(id+"F0.imprint","IMPRINT",EDGE,{"derivedFrom":sQuery(id+"F0.wireOp",EDGE,"E3")}),1.0]])]});
            var Q8;
            Q8=makeQuery(id+"F0.imprint","IMPRINT",FACE,{"disambiguationData":[TD([[makeQuery(id+"F0.imprint","IMPRINT",EDGE,{"derivedFrom":sQuery(id+"F0.wireOp",EDGE,"E26")}),1.0]])]});
            var Q9;
            Q9=makeQuery(id+"F0.imprint","IMPRINT",FACE,{"disambiguationData":[TD([[makeQuery(id+"F0.imprint","IMPRINT",EDGE,{"derivedFrom":sQuery(id+"F0.wireOp",EDGE,"E23")}),1.0]])]});
            extrude(context, id + "F2", {"entities" : qUnion([Q0, Q1, Q2, Q3, Q4, Q5, Q6, Q7, Q8, Q9]), "operationType" : NewBodyOperationType.ADD, "oppositeDirection" : true, "depth" : 3.8 * mm});
        }
    });
